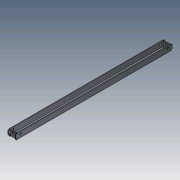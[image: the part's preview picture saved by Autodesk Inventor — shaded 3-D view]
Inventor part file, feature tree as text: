
AUTODESK INVENTOR PART (.ipt)
format: ipt  version: 2015 (Build 190159000, 159)  size: 307,712 bytes
history: native  units: mm
features: other x10, sheet_metal_op x9, sketch x8, plane x1
ambient origin geometry x8: Origin, YZ Plane, XZ Plane, XY Plane, X Axis, Y Axis, Z Axis, Center Point
bodies: Solid1 (feature_tree)
feature tree (28):
  sheet_metal_op  "Face1"
  sheet_metal_op  "Flange1"
  sheet_metal_op  "Flange2"
  plane  "Work Plane1"
  sheet_metal_op  "Flange5"
  sheet_metal_op  "Flange6"
  sketch  "Sketch1"  dims[d2=34.0mm]
  other  "Plate1"
  sketch  "Sketch2"  dims[d3=768.0mm]
  other  "Plate2"
  sheet_metal_op  "Bend1"
  sketch  "Sketch3"  dims[d4=0.001mm]
  other  "Plate3"
  sheet_metal_op  "Bend2"
  other  "FlatPattern"
  sketch  "Sketch7"  dims[d5=-5.0mm d6=-5.0mm]
  sketch  "Sketch8"  dims[d7=0.5mm]
  other  "Plate6"
  sheet_metal_op  "Bend5"
  sketch  "Sketch9"  dims[d8=4.5mm]
  other  "Plate7"
  sheet_metal_op  "Bend6"
  sketch  "Sketch10"  dims[d9=6.0mm]
  sketch  "Sketch11"  dims[d10=0.001mm d11=27.0mm d12=90.0deg d13=0.001mm d14=-5.0mm d15=-5.0mm d16=0.5mm d17=4.5mm d18=6.0mm d19=0.001mm d20=27.0mm d21=90.0deg d22=0.001mm d47=11.0mm d48=11.0mm d49=22.0mm d50=10.0mm d51=22.0mm d52=10.0mm d53=3.0mm d54=0.0mm d55=1.0mm d56=3.0mm d57=3.0mm d58=1.0mm d59=3.0mm d60=3.0mm d61=34.0mm d62=1.0mm d63=0.5mm d64=4.5mm d65=6.0mm d66=0.001mm d67=27.0mm d68=90.0deg d69=0.001mm d70=0.5mm d71=4.5mm d72=6.0mm d73=0.001mm d74=27.0mm d75=90.0deg d76=0.001mm d77=9.0mm d78=13.5mm d79=7.0mm d80=3.0mm d81=0.0mm d82=5.0mm d83=3.0mm d84=5.0mm d85=3.0mm d86=3.0mm d87=0.0mm d0=3.0mm]
  other  "Cut2"
  other  "Cut3"
  other  "Cut4"
  other  "FlatPatternExtrusion2"
